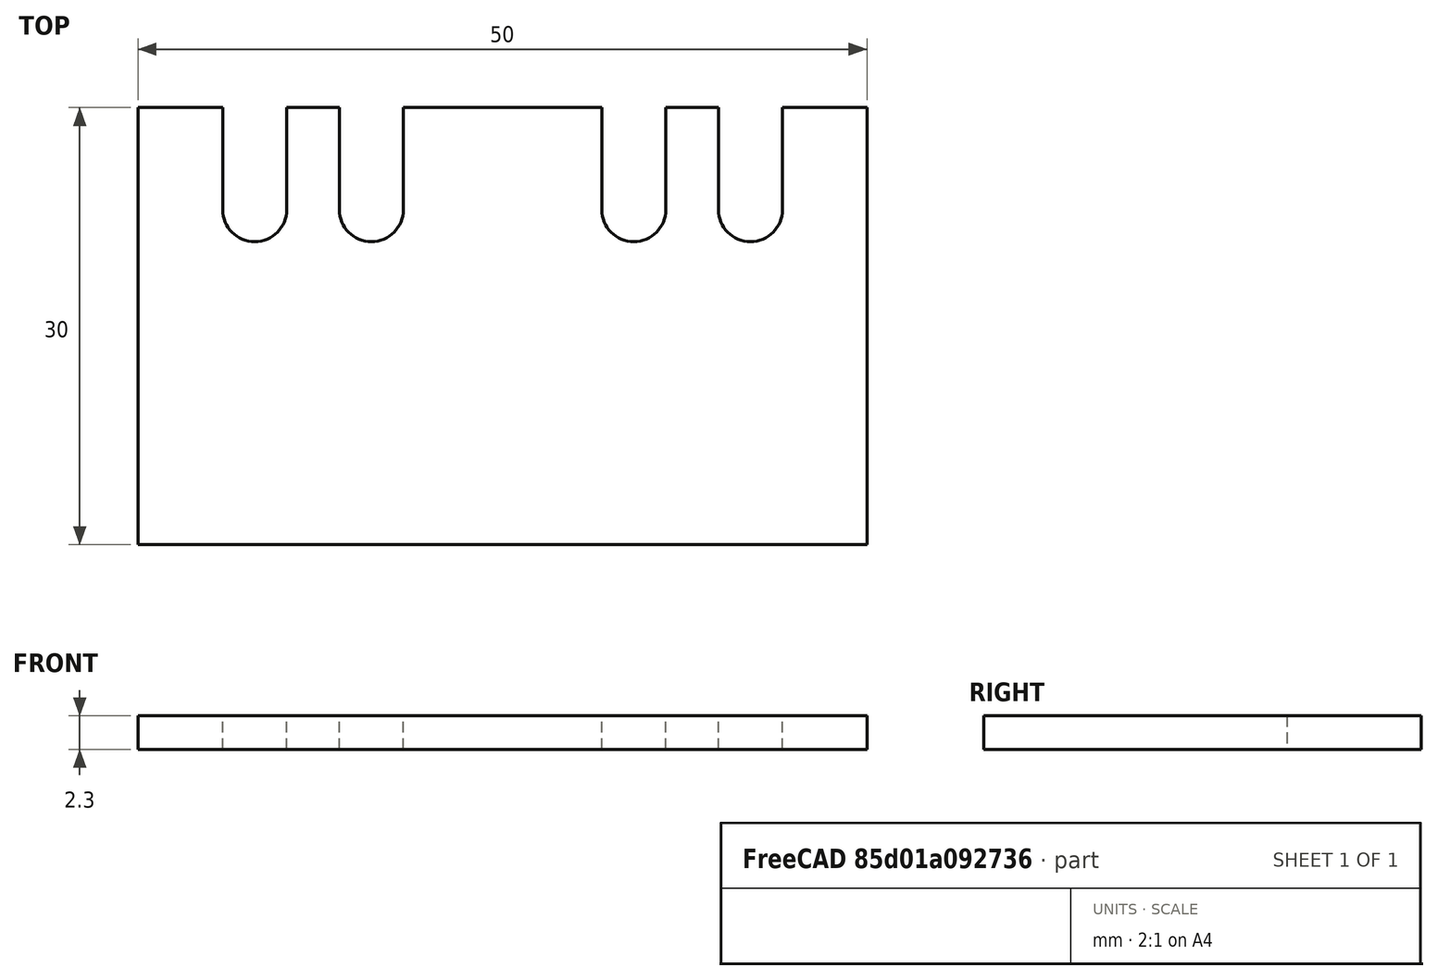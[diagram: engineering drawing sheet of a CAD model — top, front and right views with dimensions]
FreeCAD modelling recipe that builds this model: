
FCSTD DOCUMENT  (FreeCAD 0.19R24291 (Git))
Label: ResponseBox_testPlate2b
License: All rights reserved
LicenseURL: http://en.wikipedia.org/wiki/All_rights_reserved
objects: Sketcher::SketchObject×1, PartDesign::Pad×1, PartDesign::Body×1
note: 4 computed .brp shape members not serialized (recipe doc carries the construction recipe); baked Part::Feature solids carry a one-line shape summary decoded from their .brp

FEATURE [Sketcher::SketchObject] Sketch
  FullyConstrained = true
  MapMode = 5
  Support = -> [XY_Plane]
  sketch-geometry (20):
    g0: LineSegment StartX=0 StartY=0 StartZ=0 EndX=50 EndY=0 EndZ=0
    g1: LineSegment StartX=50 StartY=0 StartZ=0 EndX=50 EndY=30 EndZ=0
    g2: LineSegment StartX=0 StartY=30 StartZ=0 EndX=0 EndY=0 EndZ=0
    g3: ArcOfCircle CenterX=8 CenterY=23 CenterZ=0 NormalX=0 NormalY=0 NormalZ=1 AngleXU=0 Radius=2.2 StartAngle=3.14159 EndAngle=6.28319
    g4: ArcOfCircle CenterX=16 CenterY=23 CenterZ=0 NormalX=0 NormalY=0 NormalZ=1 AngleXU=0 Radius=2.2 StartAngle=3.14159 EndAngle=6.28319
    g5: ArcOfCircle CenterX=34 CenterY=23 CenterZ=0 NormalX=0 NormalY=0 NormalZ=1 AngleXU=0 Radius=2.2 StartAngle=3.14159 EndAngle=6.28319
    g6: ArcOfCircle CenterX=42 CenterY=23 CenterZ=0 NormalX=0 NormalY=0 NormalZ=1 AngleXU=0 Radius=2.2 StartAngle=3.14159 EndAngle=6.28319
    g7: LineSegment StartX=10.2 StartY=30 StartZ=0 EndX=10.2 EndY=23 EndZ=0
    g8: LineSegment StartX=5.8 StartY=23 StartZ=0 EndX=5.8 EndY=30 EndZ=0
    g9: LineSegment StartX=18.2 StartY=30 StartZ=0 EndX=18.2 EndY=23 EndZ=0
    g10: LineSegment StartX=13.8 StartY=23 StartZ=0 EndX=13.8 EndY=30 EndZ=0
    g11: LineSegment StartX=36.2 StartY=30 StartZ=0 EndX=36.2 EndY=23 EndZ=0
    g12: LineSegment StartX=31.8 StartY=23 StartZ=0 EndX=31.8 EndY=30 EndZ=0
    g13: LineSegment StartX=44.2 StartY=30 StartZ=0 EndX=44.2 EndY=23 EndZ=0
    g14: LineSegment StartX=39.8 StartY=23 StartZ=0 EndX=39.8 EndY=30 EndZ=0
    g15: LineSegment StartX=5.8 StartY=30 StartZ=0 EndX=0 EndY=30 EndZ=0
    g16: LineSegment StartX=13.8 StartY=30 StartZ=0 EndX=10.2 EndY=30 EndZ=0
    g17: LineSegment StartX=31.8 StartY=30 StartZ=0 EndX=18.2 EndY=30 EndZ=0
    g18: LineSegment StartX=39.8 StartY=30 StartZ=0 EndX=36.2 EndY=30 EndZ=0
    g19: LineSegment StartX=44.2 StartY=30 StartZ=0 EndX=50 EndY=30 EndZ=0
  constraints (63):
    c: Coincident(g0,g1)
    c: Coincident(g15,g2)
    c: Coincident(g2,g0)
    c: Horizontal(g0)
    c: Vertical(g1)
    c: Vertical(g2)
    c: DistanceX(g15,g1) = 50
    c: DistanceY(g2,g2) = 30
    c: Coincident(g0,g-1)
    c: Radius(g3) = 2.2
    c: Radius(g4) = 2.2
    c: Radius(g5) = 2.2
    c: Radius(g6) = 2.2
    c: DistanceX(g3,g4) = 8
    c: DistanceX(g5,g6) = 8
    c: DistanceY(g4,g3) = 0
    c: DistanceY(g5,g6) = 0
    c: DistanceY(g3,g15) = 7
    c: DistanceY(g5,g4) = 0
    c: DistanceX(g15,g3) = 8
    c: DistanceX(g6,g1) = 8
    c: Vertical(g7)
    c: Vertical(g8)
    c: Vertical(g9)
    c: Vertical(g10)
    c: Vertical(g11)
    c: Vertical(g12)
    c: Vertical(g13)
    c: Vertical(g14)
    c: DistanceY(g3,g7) = 0
    c: DistanceY(g4,g9) = 0
    c: DistanceY(g5,g11) = 0
    c: DistanceY(g6,g13) = 0
    c: DistanceY(g13,g1) = 0
    c: DistanceY(g11,g14) = 0
    c: DistanceY(g7,g10) = 0
    c: Coincident(g3,g7)
    c: Coincident(g4,g9)
    c: Coincident(g5,g11)
    c: Coincident(g6,g13)
    c: Coincident(g3,g8)
    c: Coincident(g4,g10)
    c: Coincident(g5,g12)
    c: Coincident(g6,g14)
    c: DistanceY(g8,g7) = 0
    c: DistanceY(g10,g9) = 0
    c: DistanceY(g11,g12) = 0
    c: DistanceY(g14,g13) = 0
    c: DistanceY(g13,g13) = 7
    c: DistanceY(g14,g14) = 7
    c: DistanceY(g12,g12) = 7
    c: DistanceY(g9,g9) = 7
    c: DistanceY(g10,g10) = 7
    c: DistanceY(g8,g8) = 7
    c: Coincident(g19,g13)
    c: Coincident(g1,g19)
    c: Coincident(g17,g9)
    c: Coincident(g17,g12)
    c: Coincident(g8,g15)
    c: Coincident(g7,g16)
    c: Coincident(g10,g16)
    c: Coincident(g11,g18)
    c: Coincident(g14,g18)
FEATURE [PartDesign::Pad] Pad
  Direction = (1,1,1)
  Length = 2.3
  Length2 = 100
  Profile = -> Sketch
  Type = 0
FEATURE [PartDesign::Body] Body
  Group = -> [Sketch,Pad]
  Origin = -> Origin
  Tip = -> Pad
